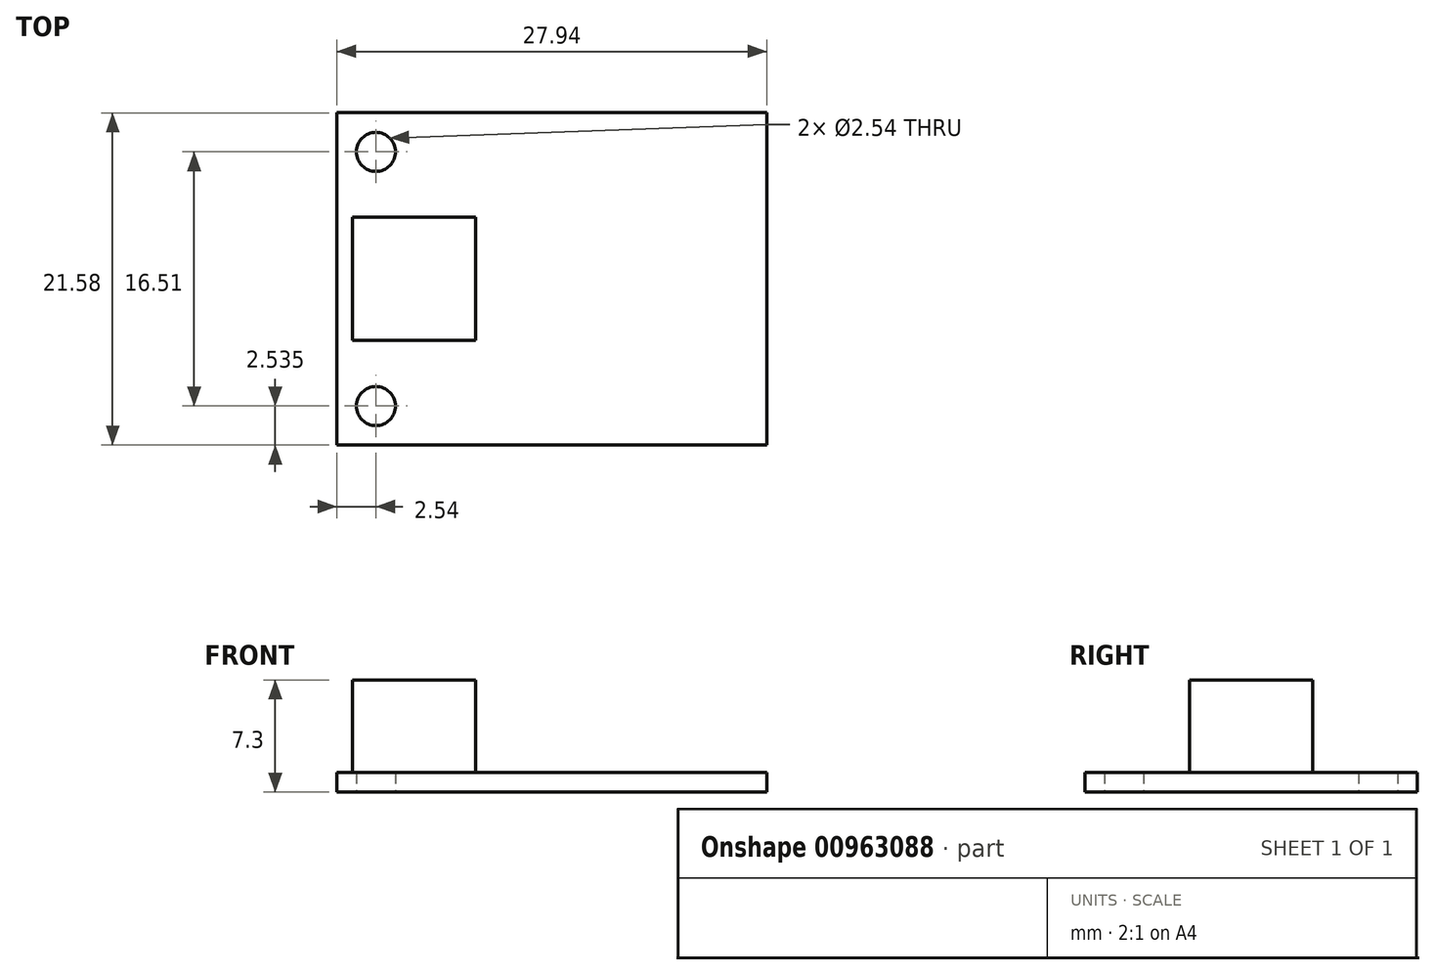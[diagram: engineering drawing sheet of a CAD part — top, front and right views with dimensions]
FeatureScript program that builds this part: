
annotation { "Feature Type Name" : "Feature", "Feature Type Description" : "" }
export const myFeature = defineFeature(function(context is Context, id is Id, definition is map)
    precondition{}
    {
        {
            var Q0;
            Q0=qCreatedBy(makeId("Top.planeOp"),FACE);
            var sketch = newSketch(context, id + "F0", { "sketchPlane" : qUnion([Q0])});
            skLineSegment(sketch, "E0.bottom", {"start": v(-13.97, 10.8) * mm, "end": v(13.97, 10.8) * mm});
            skLineSegment(sketch, "E0.top", {"start": v(-13.97, -10.8) * mm, "end": v(13.97, -10.8) * mm});
            skLineSegment(sketch, "E0.left", {"start": v(-13.97, 10.8) * mm, "end": v(-13.97, -10.8) * mm});
            skLineSegment(sketch, "E0.right", {"start": v(13.97, 10.8) * mm, "end": v(13.97, -10.8) * mm});
            skLineSegment(sketch, "E1", {"start": v(-13.97, 10.8) * mm, "end": v(13.97, -10.8) * mm, "construction": true});
            skCircle(sketch, "E2", {"center": v(-11.43, 8.25) * mm, "radius": 1.27 * mm});
            skCircle(sketch, "E3", {"center": v(-11.43, -8.25) * mm, "radius": 1.27 * mm});
            skLineSegment(sketch, "E4", {"start": v(0, 0) * mm, "end": v(-17.16, 0) * mm, "construction": true});
            skSolve(sketch);
        }
        {
            var Q0;
            Q0 = qSketchRegion(id + "F0", true);
            extrude(context, id + "F1", {"entities" : qUnion([Q0]), "depth" : 1.3 * mm, "offsetDistance" : 25 * mm, "symmetric" : true});
        }
        {
            var Q0;
            Q0=makeQuery(id+"F1.opExtrude","CAP_FACE",FACE,{"disambiguationData":[OSD([sQuery(id+"F0.wireOp",EDGE,"E0.bottom"),sQuery(id+"F0.wireOp",EDGE,"E0.top"),sQuery(id+"F0.wireOp",EDGE,"E0.left"),sQuery(id+"F0.wireOp",EDGE,"E0.right"),sQuery(id+"F0.wireOp",EDGE,"E2"),sQuery(id+"F0.wireOp",EDGE,"E3")])],"isStart":false});
            var sketch = newSketch(context, id + "F2", { "sketchPlane" : qUnion([Q0])});
            skLineSegment(sketch, "E5.bottom", {"start": v(-12.97, 4) * mm, "end": v(-4.97, 4) * mm});
            skLineSegment(sketch, "E5.top", {"start": v(-12.97, -4) * mm, "end": v(-4.97, -4) * mm});
            skLineSegment(sketch, "E5.left", {"start": v(-12.97, 4) * mm, "end": v(-12.97, -4) * mm});
            skLineSegment(sketch, "E5.right", {"start": v(-4.97, 4) * mm, "end": v(-4.97, -4) * mm});
            skLineSegment(sketch, "E6", {"start": v(-4.97, 0) * mm, "end": v(0, 0) * mm, "construction": true});
            skSolve(sketch);
        }
        {
            var Q0;
            Q0 = qSketchRegion(id + "F2", true);
            extrude(context, id + "F3", {"entities" : qUnion([Q0]), "operationType" : NewBodyOperationType.ADD, "depth" : 6 * mm, "offsetDistance" : 25 * mm});
        }
    });
